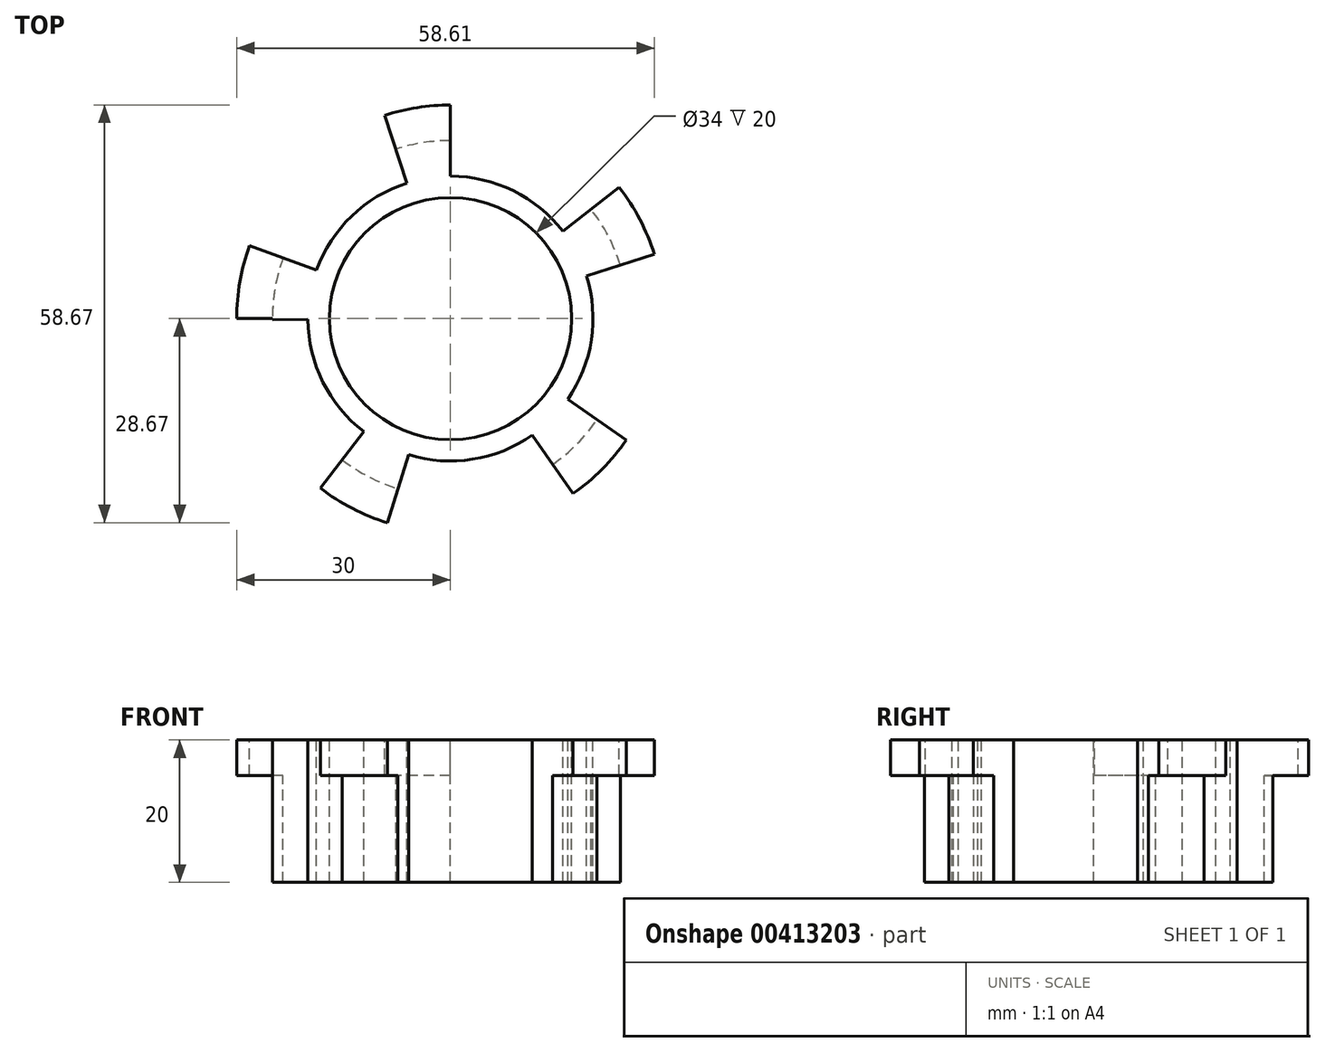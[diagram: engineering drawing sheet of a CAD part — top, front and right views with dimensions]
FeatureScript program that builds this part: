
annotation { "Feature Type Name" : "Feature", "Feature Type Description" : "" }
export const myFeature = defineFeature(function(context is Context, id is Id, definition is map)
    precondition{}
    {
        {
            var Q0;
            Q0=qCreatedBy(makeId("Top.planeOp"),FACE);
            var sketch = newSketch(context, id + "F0", { "sketchPlane" : qUnion([Q0])});
            skCircle(sketch, "E0", {"center": v(0, 0) * mm, "radius": 25 * mm});
            skCircle(sketch, "E1", {"center": v(0, 0) * mm, "radius": 15 * mm});
            skSolve(sketch);
        }
        {
            var Q0;
            Q0=makeQuery(id+"F0.imprint","IMPRINT",FACE,{"disambiguationData":[TD([[makeQuery(id+"F0.imprint","IMPRINT",EDGE,{"derivedFrom":sQuery(id+"F0.wireOp",EDGE,"E0")}),1.0]])]});
            extrude(context, id + "F1", {"entities" : qUnion([Q0]), "depth" : 80 * mm});
        }
        {
            var Q0;
            Q0=makeQuery(id+"F1.opExtrude","CAP_FACE",FACE,{"disambiguationData":[OSD([sQuery(id+"F0.wireOp",EDGE,"E0"),sQuery(id+"F0.wireOp",EDGE,"E1")])],"isStart":false});
            var sketch = newSketch(context, id + "F2", { "sketchPlane" : qUnion([Q0])});
            skLineSegment(sketch, "E2", {"start": v(0, 20) * mm, "end": v(0, 25) * mm});
            skArc(sketch, "E3", {"start": v(19.73, 15.35) * mm, "mid": v(10.98, 22.46) * mm, "end": v(0, 25) * mm});
            skLineSegment(sketch, "E4", {"start": v(15.79, 12.28) * mm, "end": v(19.73, 15.35) * mm});
            skArc(sketch, "E5.0", {"start": v(15.79, 12.28) * mm, "mid": v(8.79, 17.97) * mm, "end": v(0, 20) * mm});
            skLineSegment(sketch, "E6.1.0", {"start": v(19.07, 6.01) * mm, "end": v(23.84, 7.52) * mm});
            skArc(sketch, "E6.1.1", {"start": v(16.46, -11.37) * mm, "mid": v(19.78, -2.98) * mm, "end": v(19.07, 6.01) * mm});
            skLineSegment(sketch, "E6.1.2", {"start": v(16.46, -11.37) * mm, "end": v(20.57, -14.2) * mm});
            skArc(sketch, "E6.1.3", {"start": v(20.57, -14.2) * mm, "mid": v(24.72, -3.72) * mm, "end": v(23.84, 7.52) * mm});
            skLineSegment(sketch, "E6.2.0", {"start": v(11.47, -16.38) * mm, "end": v(14.34, -20.48) * mm});
            skArc(sketch, "E6.2.1", {"start": v(-5.9, -19.11) * mm, "mid": v(3.1, -19.76) * mm, "end": v(11.47, -16.38) * mm});
            skLineSegment(sketch, "E6.2.2", {"start": v(-5.9, -19.11) * mm, "end": v(-7.36, -23.9) * mm});
            skArc(sketch, "E6.2.3", {"start": v(-7.36, -23.9) * mm, "mid": v(3.88, -24.7) * mm, "end": v(14.34, -20.48) * mm});
            skLineSegment(sketch, "E6.3.0", {"start": v(-12.18, -15.87) * mm, "end": v(-15.22, -19.83) * mm});
            skArc(sketch, "E6.3.1", {"start": v(-20, -0.13) * mm, "mid": v(-17.9, -8.9) * mm, "end": v(-12.18, -15.87) * mm});
            skLineSegment(sketch, "E6.3.2", {"start": v(-20, -0.13) * mm, "end": v(-25, -0.16) * mm});
            skArc(sketch, "E6.3.3", {"start": v(-25, -0.16) * mm, "mid": v(-22.39, -11.13) * mm, "end": v(-15.22, -19.83) * mm});
            skLineSegment(sketch, "E6.4.0", {"start": v(-18.8, 6.84) * mm, "end": v(-23.5, 8.55) * mm});
            skArc(sketch, "E6.4.1", {"start": v(-6.14, 19.03) * mm, "mid": v(-13.88, 14.4) * mm, "end": v(-18.8, 6.84) * mm});
            skLineSegment(sketch, "E6.4.2", {"start": v(-6.14, 19.03) * mm, "end": v(-7.67, 23.8) * mm});
            skArc(sketch, "E6.4.3", {"start": v(-7.67, 23.8) * mm, "mid": v(-17.35, 18) * mm, "end": v(-23.5, 8.55) * mm});
            skLineSegment(sketch, "E6.anchor1", {"start": v(0, 0) * mm, "end": v(0, 20) * mm, "construction": true});
            skLineSegment(sketch, "E6.anchor2", {"start": v(0, 0) * mm, "end": v(-18.8, 6.84) * mm, "construction": true});
            skSolve(sketch);
        }
        {
            var Q0;
            {var subQ0=sQuery(id+"F2.wireOp",EDGE,"E3");Q0=makeQuery(id+"F2.imprint","IMPRINT",FACE,{"disambiguationData":[TD([[makeQuery(id+"F2.imprint","IMPRINT",EDGE,{"derivedFrom":subQ0}),1.0]])]});}
            var Q1;
            Q1=makeQuery(id+"F2.imprint","IMPRINT",FACE,{"disambiguationData":[TD([[makeQuery(id+"F2.imprint","IMPRINT",EDGE,{"derivedFrom":sQuery(id+"F2.wireOp",EDGE,"E6.4.0")}),-1.0]])]});
            var Q2;
            Q2=makeQuery(id+"F2.imprint","IMPRINT",FACE,{"disambiguationData":[TD([[makeQuery(id+"F2.imprint","IMPRINT",EDGE,{"derivedFrom":sQuery(id+"F2.wireOp",EDGE,"E6.3.0")}),-1.0]])]});
            var Q3;
            Q3=makeQuery(id+"F2.imprint","IMPRINT",FACE,{"disambiguationData":[TD([[makeQuery(id+"F2.imprint","IMPRINT",EDGE,{"derivedFrom":sQuery(id+"F2.wireOp",EDGE,"E6.2.0")}),-1.0]])]});
            var Q4;
            Q4=makeQuery(id+"F2.imprint","IMPRINT",FACE,{"disambiguationData":[TD([[makeQuery(id+"F2.imprint","IMPRINT",EDGE,{"derivedFrom":sQuery(id+"F2.wireOp",EDGE,"E6.1.0")}),-1.0]])]});
            extrude(context, id + "F3", {"entities" : qUnion([Q0, Q1, Q2, Q3, Q4]), "operationType" : NewBodyOperationType.REMOVE, "endBound" : BoundingType.THROUGH_ALL, "oppositeDirection" : true, "depth" : 25 * mm});
        }
        {
            var Q0;
            Q0=makeQuery(id+"F1.opExtrude","CAP_FACE",FACE,{"disambiguationData":[OSD([sQuery(id+"F0.wireOp",EDGE,"E0"),sQuery(id+"F0.wireOp",EDGE,"E1")])],"isStart":false});
            var sketch = newSketch(context, id + "F4", { "sketchPlane" : qUnion([Q0])});
            skCircle(sketch, "E7", {"center": v(0, 0) * mm, "radius": 25 * mm});
            skCircle(sketch, "E8.0", {"center": v(0, 0) * mm, "radius": 30 * mm});
            skLineSegment(sketch, "E9", {"start": v(0, 0) * mm, "end": v(-28.2, 10.26) * mm});
            skLineSegment(sketch, "E10", {"start": v(-30, 0) * mm, "end": v(0, 0) * mm});
            skLineSegment(sketch, "E11", {"start": v(0, 0) * mm, "end": v(-9.2, 28.55) * mm});
            skLineSegment(sketch, "E12", {"start": v(0, 0) * mm, "end": v(0, 30) * mm});
            skLineSegment(sketch, "E13", {"start": v(0, 0) * mm, "end": v(23.68, 18.42) * mm});
            skLineSegment(sketch, "E14", {"start": v(0, 0) * mm, "end": v(28.61, 9.02) * mm});
            skLineSegment(sketch, "E15", {"start": v(0, 0) * mm, "end": v(-18.26, -23.8) * mm});
            skLineSegment(sketch, "E16", {"start": v(0, 0) * mm, "end": v(-8.84, -28.67) * mm});
            skLineSegment(sketch, "E17", {"start": v(0, 0) * mm, "end": v(17.2, -24.57) * mm});
            skLineSegment(sketch, "E18", {"start": v(0, 0) * mm, "end": v(24.69, -17.05) * mm});
            skSolve(sketch);
        }
        {
            var Q0;
            {var subQ0=sQuery(id+"F4.wireOp",EDGE,"E13");var subQ1=sQuery(id+"F4.wireOp",EDGE,"E7");var subQ2=makeQuery(id+"F4.imprint","INTERSECT",VERTEX,{"derivedFrom":[subQ1,subQ0]});Q0=makeQuery(id+"F4.imprint","IMPRINT",FACE,{"disambiguationData":[TD([[makeQuery(id+"F4.imprint","IMPRINT",EDGE,{"disambiguationData":[TD([[subQ2,1.0]])],"derivedFrom":subQ1}),-1.0]])]});}
            var Q1;
            {var subQ0=sQuery(id+"F4.wireOp",EDGE,"E12");var subQ1=sQuery(id+"F4.wireOp",EDGE,"E7");var subQ2=makeQuery(id+"F4.imprint","INTERSECT",VERTEX,{"derivedFrom":[subQ1,subQ0]});Q1=makeQuery(id+"F4.imprint","IMPRINT",FACE,{"disambiguationData":[TD([[makeQuery(id+"F4.imprint","IMPRINT",EDGE,{"disambiguationData":[TD([[subQ2,-1.0]])],"derivedFrom":subQ1}),-1.0]])]});}
            var Q2;
            {var subQ0=sQuery(id+"F4.wireOp",EDGE,"E9");var subQ1=sQuery(id+"F4.wireOp",EDGE,"E7");var subQ2=makeQuery(id+"F4.imprint","INTERSECT",VERTEX,{"derivedFrom":[subQ1,subQ0]});Q2=makeQuery(id+"F4.imprint","IMPRINT",FACE,{"disambiguationData":[TD([[makeQuery(id+"F4.imprint","IMPRINT",EDGE,{"disambiguationData":[TD([[subQ2,-1.0]])],"derivedFrom":subQ1}),-1.0]])]});}
            var Q3;
            {var subQ0=sQuery(id+"F4.wireOp",EDGE,"E16");var subQ1=sQuery(id+"F4.wireOp",EDGE,"E7");var subQ2=makeQuery(id+"F4.imprint","INTERSECT",VERTEX,{"derivedFrom":[subQ1,subQ0]});Q3=makeQuery(id+"F4.imprint","IMPRINT",FACE,{"disambiguationData":[TD([[makeQuery(id+"F4.imprint","IMPRINT",EDGE,{"disambiguationData":[TD([[subQ2,1.0]])],"derivedFrom":subQ1}),-1.0]])]});}
            var Q4;
            {var subQ0=sQuery(id+"F4.wireOp",EDGE,"E18");var subQ1=sQuery(id+"F4.wireOp",EDGE,"E7");var subQ2=makeQuery(id+"F4.imprint","INTERSECT",VERTEX,{"derivedFrom":[subQ1,subQ0]});Q4=makeQuery(id+"F4.imprint","IMPRINT",FACE,{"disambiguationData":[TD([[makeQuery(id+"F4.imprint","IMPRINT",EDGE,{"disambiguationData":[TD([[subQ2,1.0]])],"derivedFrom":subQ1}),-1.0]])]});}
            var Q5;
            {var subQ1=makeQuery(id+"F3.boolean.opBoolean","COPY",EDGE,{"derivedFrom":makeQuery(id+"F3.opExtrude","CAP_EDGE",EDGE,{"disambiguationData":[OSD([sQuery(id+"F2.wireOp",EDGE,"E6.4.1")])],"isStart":true})});Q5=makeQuery(id+"F4.imprint","IMPRINT",FACE,{"disambiguationData":[TD([[makeQuery(id+"F4.imprint","IMPRINT",EDGE,{"derivedFrom":subQ1}),1.0]])]});}
            var Q6;
            {var subQ1=makeQuery(id+"F3.boolean.opBoolean","COPY",EDGE,{"derivedFrom":makeQuery(id+"F3.opExtrude","CAP_EDGE",EDGE,{"disambiguationData":[OSD([sQuery(id+"F2.wireOp",EDGE,"E5.0")])],"isStart":true})});Q6=makeQuery(id+"F4.imprint","IMPRINT",FACE,{"disambiguationData":[TD([[makeQuery(id+"F4.imprint","IMPRINT",EDGE,{"derivedFrom":subQ1}),1.0]])]});}
            var Q7;
            {var subQ1=makeQuery(id+"F3.boolean.opBoolean","COPY",EDGE,{"derivedFrom":makeQuery(id+"F3.opExtrude","CAP_EDGE",EDGE,{"disambiguationData":[OSD([sQuery(id+"F2.wireOp",EDGE,"E6.1.1")])],"isStart":true})});Q7=makeQuery(id+"F4.imprint","IMPRINT",FACE,{"disambiguationData":[TD([[makeQuery(id+"F4.imprint","IMPRINT",EDGE,{"derivedFrom":subQ1}),1.0]])]});}
            var Q8;
            {var subQ1=makeQuery(id+"F3.boolean.opBoolean","COPY",EDGE,{"derivedFrom":makeQuery(id+"F3.opExtrude","CAP_EDGE",EDGE,{"disambiguationData":[OSD([sQuery(id+"F2.wireOp",EDGE,"E6.2.1")])],"isStart":true})});Q8=makeQuery(id+"F4.imprint","IMPRINT",FACE,{"disambiguationData":[TD([[makeQuery(id+"F4.imprint","IMPRINT",EDGE,{"derivedFrom":subQ1}),1.0]])]});}
            extrude(context, id + "F5", {"entities" : qUnion([Q0, Q1, Q2, Q3, Q4, Q5, Q6, Q7, Q8]), "operationType" : NewBodyOperationType.ADD, "oppositeDirection" : true, "depth" : 5 * mm});
        }
        {
            var Q0;
            Q0=qCreatedBy(makeId("Top.planeOp"),FACE);
            var sketch = newSketch(context, id + "F6", { "sketchPlane" : qUnion([Q0])});
            skLineSegment(sketch, "E19.bottom", {"start": v(-51.28, -39.37) * mm, "end": v(54.64, -39.37) * mm});
            skLineSegment(sketch, "E19.top", {"start": v(-51.28, 40.3) * mm, "end": v(54.64, 40.3) * mm});
            skLineSegment(sketch, "E19.left", {"start": v(-51.28, -39.37) * mm, "end": v(-51.28, 40.3) * mm});
            skLineSegment(sketch, "E19.right", {"start": v(54.64, -39.37) * mm, "end": v(54.64, 40.3) * mm});
            skSolve(sketch);
        }
        {
            var Q0;
            Q0 = qSketchRegion(id + "F6", true);
            extrude(context, id + "F7", {"entities" : qUnion([Q0]), "operationType" : NewBodyOperationType.REMOVE, "depth" : 60 * mm});
        }
        {
            var Q0;
            {var subQ0=sQuery(id+"F4.wireOp",EDGE,"E8.0");var subQ1=sQuery(id+"F4.wireOp",EDGE,"E7");Q0=makeQuery(id+"F5.boolean.opBoolean","MERGE",FACE,{"derivedFrom":[makeQuery(id+"F1.opExtrude","CAP_FACE",FACE,{"disambiguationData":[OSD([sQuery(id+"F0.wireOp",EDGE,"E0"),sQuery(id+"F0.wireOp",EDGE,"E1")])],"isStart":false}),makeQuery(id+"F5.opExtrude","CAP_FACE",FACE,{"disambiguationData":[OSD([subQ1,subQ0,sQuery(id+"F4.wireOp",EDGE,"E13"),sQuery(id+"F4.wireOp",EDGE,"E14")])],"isStart":true}),makeQuery(id+"F5.opExtrude","CAP_FACE",FACE,{"disambiguationData":[OSD([subQ1,subQ0,sQuery(id+"F4.wireOp",EDGE,"E11"),sQuery(id+"F4.wireOp",EDGE,"E12")])],"isStart":true}),makeQuery(id+"F5.opExtrude","CAP_FACE",FACE,{"disambiguationData":[OSD([subQ1,subQ0,sQuery(id+"F4.wireOp",EDGE,"E9"),sQuery(id+"F4.wireOp",EDGE,"E10")])],"isStart":true}),makeQuery(id+"F5.opExtrude","CAP_FACE",FACE,{"disambiguationData":[OSD([subQ1,subQ0,sQuery(id+"F4.wireOp",EDGE,"E15"),sQuery(id+"F4.wireOp",EDGE,"E16")])],"isStart":true}),makeQuery(id+"F5.opExtrude","CAP_FACE",FACE,{"disambiguationData":[OSD([subQ1,subQ0,sQuery(id+"F4.wireOp",EDGE,"E17"),sQuery(id+"F4.wireOp",EDGE,"E18")])],"isStart":true})]});}
            var sketch = newSketch(context, id + "F8", { "sketchPlane" : qUnion([Q0])});
            skCircle(sketch, "E20.0", {"center": v(0, 0) * mm, "radius": 17 * mm});
            skSolve(sketch);
        }
        {
            var Q0;
            Q0 = qSketchRegion(id + "F8", true);
            extrude(context, id + "F9", {"entities" : qUnion([Q0]), "operationType" : NewBodyOperationType.REMOVE, "endBound" : BoundingType.THROUGH_ALL, "oppositeDirection" : true, "depth" : 25 * mm});
        }
    });
